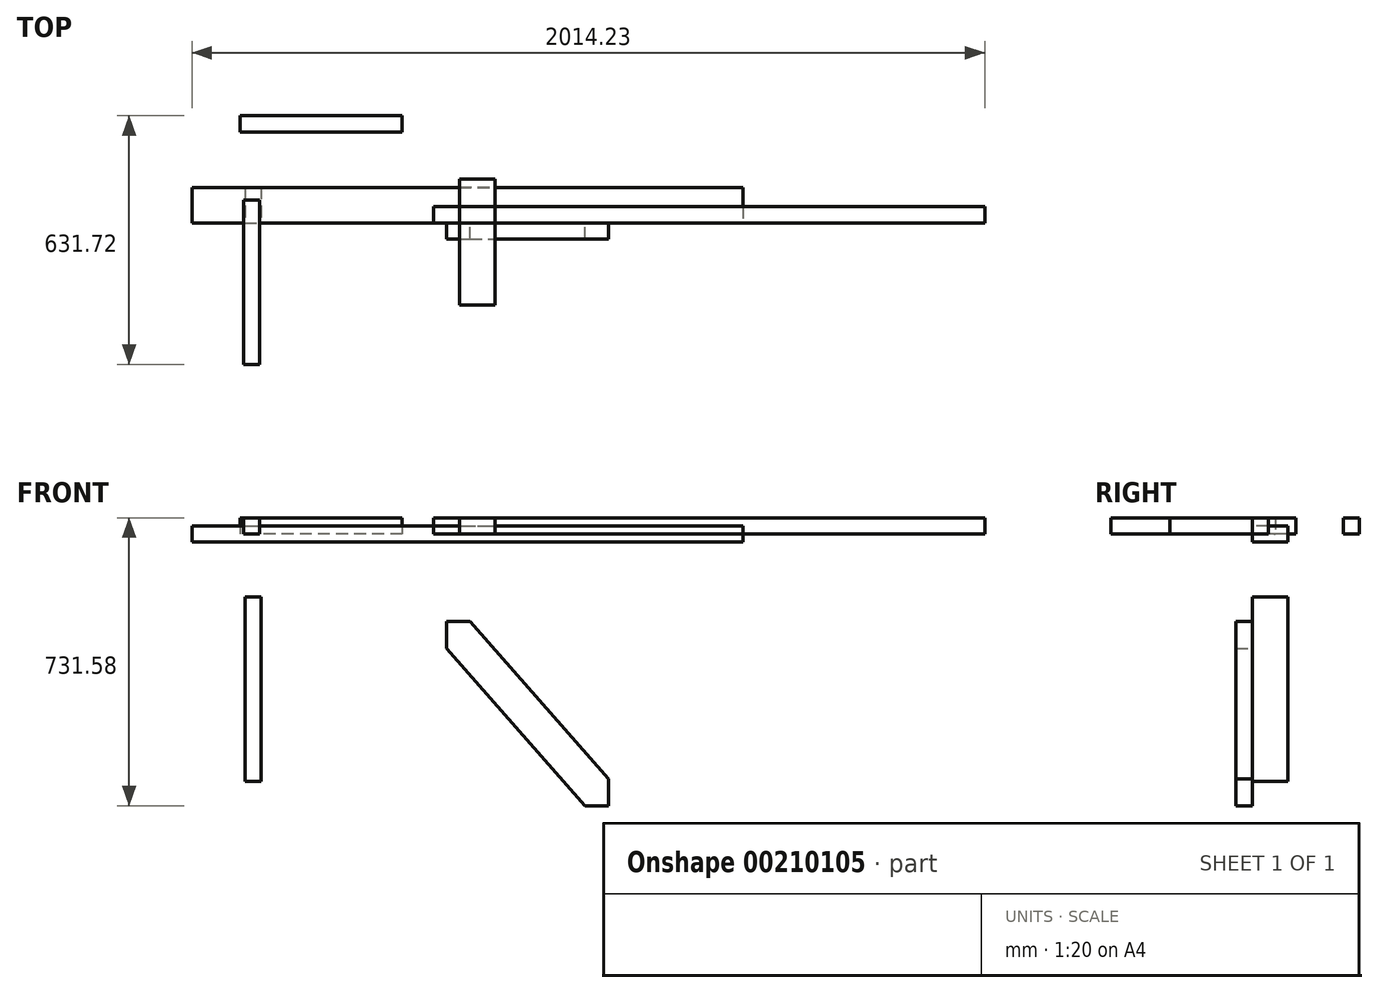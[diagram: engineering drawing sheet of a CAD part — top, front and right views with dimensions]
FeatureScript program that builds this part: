
annotation { "Feature Type Name" : "Feature", "Feature Type Description" : "" }
export const myFeature = defineFeature(function(context is Context, id is Id, definition is map)
    precondition{}
    {
        {
            var Q0;
            Q0=qCreatedBy(makeId("Top.planeOp"),FACE);
            var sketch = newSketch(context, id + "F0", { "sketchPlane" : qUnion([Q0])});
            skLineSegment(sketch, "E0", {"start": v(-85.77, 41) * mm, "end": v(1314.23, 41) * mm});
            skLineSegment(sketch, "E1", {"start": v(1314.23, 41) * mm, "end": v(1314.23, 0) * mm});
            skLineSegment(sketch, "E2", {"start": v(1314.23, 0) * mm, "end": v(-85.77, 0) * mm});
            skLineSegment(sketch, "E3", {"start": v(-85.77, 0) * mm, "end": v(-85.77, 41) * mm});
            skSolve(sketch);
        }
        {
            var Q0;
            Q0 = qSketchRegion(id + "F0", true);
            extrude(context, id + "F1", {"entities" : qUnion([Q0]), "depth" : 41 * mm, "hasDraft" : true, "draftAngle" : 0 * degree});
        }
        {
            var Q0;
            Q0=qCreatedBy(makeId("Top.planeOp"),FACE);
            var sketch = newSketch(context, id + "F2", { "sketchPlane" : qUnion([Q0])});
            skLineSegment(sketch, "E4", {"start": v(-569.36, 58.5) * mm, "end": v(-528.36, 58.5) * mm});
            skLineSegment(sketch, "E5", {"start": v(-528.36, 58.5) * mm, "end": v(-528.36, -359.5) * mm});
            skLineSegment(sketch, "E6", {"start": v(-528.36, -359.5) * mm, "end": v(-569.36, -359.5) * mm});
            skLineSegment(sketch, "E7", {"start": v(-569.36, -359.5) * mm, "end": v(-569.36, 58.5) * mm});
            skSolve(sketch);
        }
        {
            var Q0;
            Q0 = qSketchRegion(id + "F2", true);
            extrude(context, id + "F3", {"entities" : qUnion([Q0]), "depth" : 41 * mm});
        }
        {
            var Q0;
            Q0=qCreatedBy(makeId("Front.planeOp"),FACE);
            var sketch = newSketch(context, id + "F4", { "sketchPlane" : qUnion([Q0])});
            skLineSegment(sketch, "E8", {"start": v(-565.47, -160.6) * mm, "end": v(-524.47, -160.6) * mm});
            skLineSegment(sketch, "E9", {"start": v(-524.47, -160.6) * mm, "end": v(-524.47, -628.6) * mm});
            skLineSegment(sketch, "E10", {"start": v(-524.47, -628.6) * mm, "end": v(-565.47, -628.6) * mm});
            skLineSegment(sketch, "E11", {"start": v(-565.47, -628.6) * mm, "end": v(-565.47, -160.6) * mm});
            skSolve(sketch);
        }
        {
            var Q0;
            Q0 = qSketchRegion(id + "F4", true);
            extrude(context, id + "F5", {"entities" : qUnion([Q0]), "oppositeDirection" : true, "depth" : 90 * mm});
        }
        {
            var Q0;
            Q0=qCreatedBy(makeId("Front.planeOp"),FACE);
            var sketch = newSketch(context, id + "F6", { "sketchPlane" : qUnion([Q0])});
            skLineSegment(sketch, "E12", {"start": v(-700, 20.5) * mm, "end": v(700, 20.5) * mm});
            skLineSegment(sketch, "E13", {"start": v(700, 20.5) * mm, "end": v(700, -20.5) * mm});
            skLineSegment(sketch, "E14", {"start": v(700, -20.5) * mm, "end": v(-700, -20.5) * mm});
            skLineSegment(sketch, "E15", {"start": v(-700, -20.5) * mm, "end": v(-700, 20.5) * mm});
            skSolve(sketch);
        }
        {
            var Q0;
            Q0=makeQuery(id+"F6.imprint","IMPRINT",FACE,{"disambiguationData":[TD([[makeQuery(id+"F6.imprint","IMPRINT",EDGE,{"derivedFrom":sQuery(id+"F6.wireOp",EDGE,"E12")}),-1.0]])]});
            extrude(context, id + "F7", {"entities" : qUnion([Q0]), "oppositeDirection" : true, "depth" : 90 * mm});
        }
        {
            var Q0;
            Q0=qCreatedBy(makeId("Top.planeOp"),FACE);
            var sketch = newSketch(context, id + "F8", { "sketchPlane" : qUnion([Q0])});
            skLineSegment(sketch, "E16", {"start": v(-20.5, 111) * mm, "end": v(69.5, 111) * mm});
            skLineSegment(sketch, "E17", {"start": v(69.5, 111) * mm, "end": v(69.5, -209) * mm});
            skLineSegment(sketch, "E18", {"start": v(69.5, -209) * mm, "end": v(-20.5, -209) * mm});
            skLineSegment(sketch, "E19", {"start": v(-20.5, -209) * mm, "end": v(-20.5, 111) * mm});
            skSolve(sketch);
        }
        {
            var Q0;
            Q0=makeQuery(id+"F8.imprint","IMPRINT",FACE,{"disambiguationData":[TD([[makeQuery(id+"F8.imprint","IMPRINT",EDGE,{"derivedFrom":sQuery(id+"F8.wireOp",EDGE,"E16")}),-1.0]])]});
            extrude(context, id + "F9", {"entities" : qUnion([Q0]), "depth" : 41 * mm});
        }
        {
            var Q0;
            Q0=qCreatedBy(makeId("Top.planeOp"),FACE);
            var sketch = newSketch(context, id + "F10", { "sketchPlane" : qUnion([Q0])});
            skLineSegment(sketch, "E20", {"start": v(-577.98, 231.22) * mm, "end": v(-577.98, 272.22) * mm});
            skLineSegment(sketch, "E21", {"start": v(-577.98, 272.22) * mm, "end": v(-165.98, 272.22) * mm});
            skLineSegment(sketch, "E22", {"start": v(-165.98, 272.22) * mm, "end": v(-165.98, 231.22) * mm});
            skLineSegment(sketch, "E23", {"start": v(-165.98, 231.22) * mm, "end": v(-577.98, 231.22) * mm});
            skSolve(sketch);
        }
        {
            var Q0;
            Q0=makeQuery(id+"F10.imprint","IMPRINT",FACE,{"disambiguationData":[TD([[makeQuery(id+"F10.imprint","IMPRINT",EDGE,{"derivedFrom":sQuery(id+"F10.wireOp",EDGE,"E20")}),-1.0]])]});
            extrude(context, id + "F11", {"entities" : qUnion([Q0]), "depth" : 41 * mm});
        }
        {
            var Q0;
            Q0=qCreatedBy(makeId("Front.planeOp"),FACE);
            var sketch = newSketch(context, id + "F12", { "sketchPlane" : qUnion([Q0])});
            skLineSegment(sketch, "E24", {"start": v(-53.44, -290.58) * mm, "end": v(-53.44, -222.58) * mm});
            skLineSegment(sketch, "E25", {"start": v(-53.44, -222.58) * mm, "end": v(6.56, -222.58) * mm});
            skLineSegment(sketch, "E26", {"start": v(6.56, -222.58) * mm, "end": v(358.55, -622.58) * mm});
            skLineSegment(sketch, "E27", {"start": v(358.55, -622.58) * mm, "end": v(358.55, -690.58) * mm});
            skLineSegment(sketch, "E28", {"start": v(358.55, -690.58) * mm, "end": v(298.55, -690.58) * mm});
            skLineSegment(sketch, "E29", {"start": v(298.55, -690.58) * mm, "end": v(-53.44, -290.58) * mm});
            skSolve(sketch);
        }
        {
            var Q0;
            Q0 = qSketchRegion(id + "F12", true);
            extrude(context, id + "F13", {"entities" : qUnion([Q0]), "depth" : 41 * mm});
        }
    });
